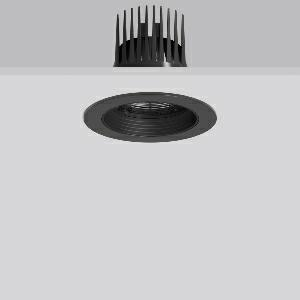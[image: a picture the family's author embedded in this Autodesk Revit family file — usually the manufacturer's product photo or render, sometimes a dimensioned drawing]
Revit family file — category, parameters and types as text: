
# Revit family: heledon_maxi_e_901761_003_2_42c7
name_source: partatom
category: Lighting Fixtures
units: mm (PartAtom-declared; Revit-internal decimal feet)

## family parameters
Cut with Voids When Loaded = No
Host = Face
Light Source = No
Part Type = Normal
Room Calculation Point = No
Round Connector Dimension = Use Diameter
Shared = No

## types (1)
- HELEDON maxi E (1 x LED Modul 927, 2550 lm, 2700)
    Apparent Load = 25 VA
    Approval mark = CE
    CIE Flux Codes = 96 100 100 100 100
    Color Rendering = 92
    Color Temperature = 2700
    Default Elevation = 1800 mm
    Description = Series: HELEDON maxi
Round recessed downlight. Housing: die-cast aluminium, powder-coated. Black plastic ring and recessed LED to prevent glare from the side. Optical assembly with lens made of plastic (polycarbonate) for the best homogeneous light distribution - can be changed without tools. Best colour rendering index Ra>90. Suitable for Recessed ceiling mounting. Installation without tools thanks to spring fastening system. Including separate LED converter with connecting cable 600 mm.High quality converter without flickering and stroboscopic effect. Through-wiring box (5 pole) available as accessory. The following accessories can be mounted without use of tools: interchangeable lenses, decorative glasses, honeycomb louvre, clear and frosted diffusers, white interchangeable plastic ring. 
Colour: deep black, matt (RAL 9005)
Diameter: 162 mm
Height: 3 mm
Cut-out diameter: 152 mm
Recess height: 200 mm
Luminaire: recess height: 135 mm
Lamp: LED
Socket: without socket
Colour temperature: 2700K
Colour rendering index (CRI): 92
System power: 25 W
Rated luminous flux: 2550 lm
Luminous efficiency: 102 lm/W
Control gear: Regulated power supply
Protection class: II
Type of protection: IP 20
    Height = 0 mm  [stored 0 ft]
    Lamp = 1 x LED Modul 927
    Lamp Light Flux = 2550 lm
    Lamp count = 1
    Length = 162 mm
    Lifetime = 50000 h
    Luminous efficacy = 102 lm/W
    Manufacturer = RZB
    ModVariant = No
    Model = 901761.003.2
    Mounting Place = Ceiling
    Mounting Type = Recessed
    Number of Poles = 1
    OnlyDefault = Yes
    Power Factor = 1
    Product Name = HELEDON maxi E
    Product group = Recessed downlights
    ProductGroupID = 402
    Protection Class = Protection class II
    Protection Degree = IP 20
    RLX_Detail_Level = 1
    RLX_Emergency_Light_Flux = 0 lm
    RLX_Emergency_Type = 0
    RLX_Emergency_Type_DB = No
    RlxData = <blob elided: 121317 chars, md5=60e7a1fa>
    Socket = socket
    Standby Power = 0 W
    System Light Flux = 2550 lm
    System Power = 25 W
    Type Comments = Product without accessories
    Type Image = 901663.003.jpg
    URL = http://relux.com
    VarID = ---
    Voltage = 230 V
    Voltage Range = 220-240 V
    Weight = 0.00 kg
    Width = 0 mm  [stored 0 ft]

note: [stored X ft] marks values corroborated as IEEE doubles in the binary element streams (Revit-internal decimal feet)

## geometry (parser evidence)
native form markers: Blend x4, Sweep x8
no freeform markers — native parametric forms only
